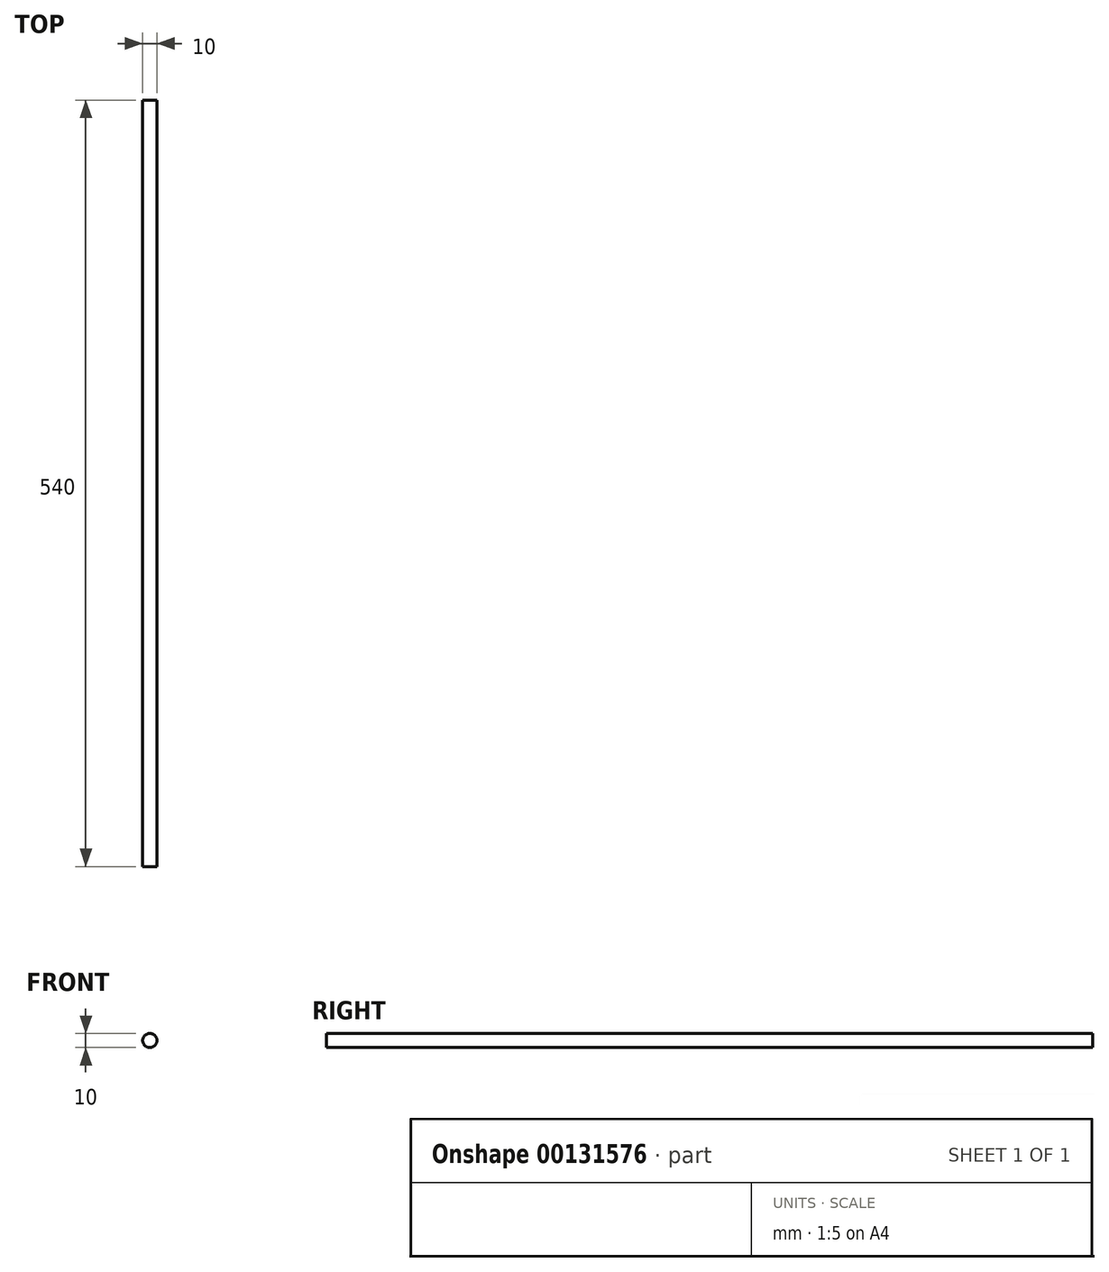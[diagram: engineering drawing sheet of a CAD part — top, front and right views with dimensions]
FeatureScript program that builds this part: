
annotation { "Feature Type Name" : "Feature", "Feature Type Description" : "" }
export const myFeature = defineFeature(function(context is Context, id is Id, definition is map)
    precondition{}
    {
        {
            var Q0;
            Q0=qCreatedBy(makeId("Front.planeOp"),FACE);
            var sketch = newSketch(context, id + "F0", { "sketchPlane" : qUnion([Q0])});
            skCircle(sketch, "E0", {"center": v(0, 0) * mm, "radius": 5 * mm});
            skSolve(sketch);
        }
        {
            var Q0;
            Q0=makeQuery(id+"F0.imprint","IMPRINT",FACE,{"disambiguationData":[TD([[makeQuery(id+"F0.imprint","IMPRINT",EDGE,{"derivedFrom":sQuery(id+"F0.wireOp",EDGE,"E0")}),1.0]])]});
            extrude(context, id + "F1", {"entities" : qUnion([Q0]), "endBound" : BoundingType.SYMMETRIC, "depth" : 540 * mm});
        }
    });
